# Revit family: S4_Surface Mounted Down Light
name_source: partatom
category: Lighting Fixtures
revit_build: Autodesk Revit MEP 2013 (Build: 20130531_2115(x64)
units: mm (PartAtom-declared; Revit-internal decimal feet)

## types (1)
- S4_Surface Mounted Down Light
    Apparent Load = 36 VA
    Default Elevation = 2800 mm  [stored 9.18635 ft]
    Description = StyliD Compact Power
    Initial Color = 3000 K
    Initial Intensity = 1943 lm
    Lamp = 1x36w
    Lamp type = lamp-types-adjustable : BBG542 1xSLED1700/830 MB-ACT
    Light Body = Light Body
    Light Loss Factor = 1
    Light Type = S4
    Load Classification = Ltg
    Manufacturer = Philips
    Model = BBG542 1xSLED1700/830 MB-ACT
    Type Comments = Recessed adjustable round LED luminaire with medium beam
    URL = http://www.ecat.lighting.philips.com
    ceiling thickness = 13 mm
    distance pivot point = 17 mm
    front rim height = 10 mm  [stored 0.0328084 ft]
    front rim inside radius = 51 mm
    front rim lenght = 152 mm  [stored 0.498688 ft]
    front rim outside radius = 76 mm  [stored 0.249344 ft]
    front rim round = Yes
    front rim square = No
    glare shield = No
    honeycomb louver = No
    instalation space radius = 66 mm  [stored 0.216535 ft]
    installation space height = 125 mm  [stored 0.410105 ft]
    outside diameter = 152 mm  [stored 0.498688 ft]
    recess diameter = 134 mm
    recess height = 250 mm  [stored 0.82021 ft]
    recess radius = 67 mm
    voltage = 230 V

note: [stored X ft] marks values corroborated as IEEE doubles in the binary element streams (Revit-internal decimal feet)

## geometry (parser evidence)
native form markers: Blend x9, Sweep x12
no freeform markers — native parametric forms only
